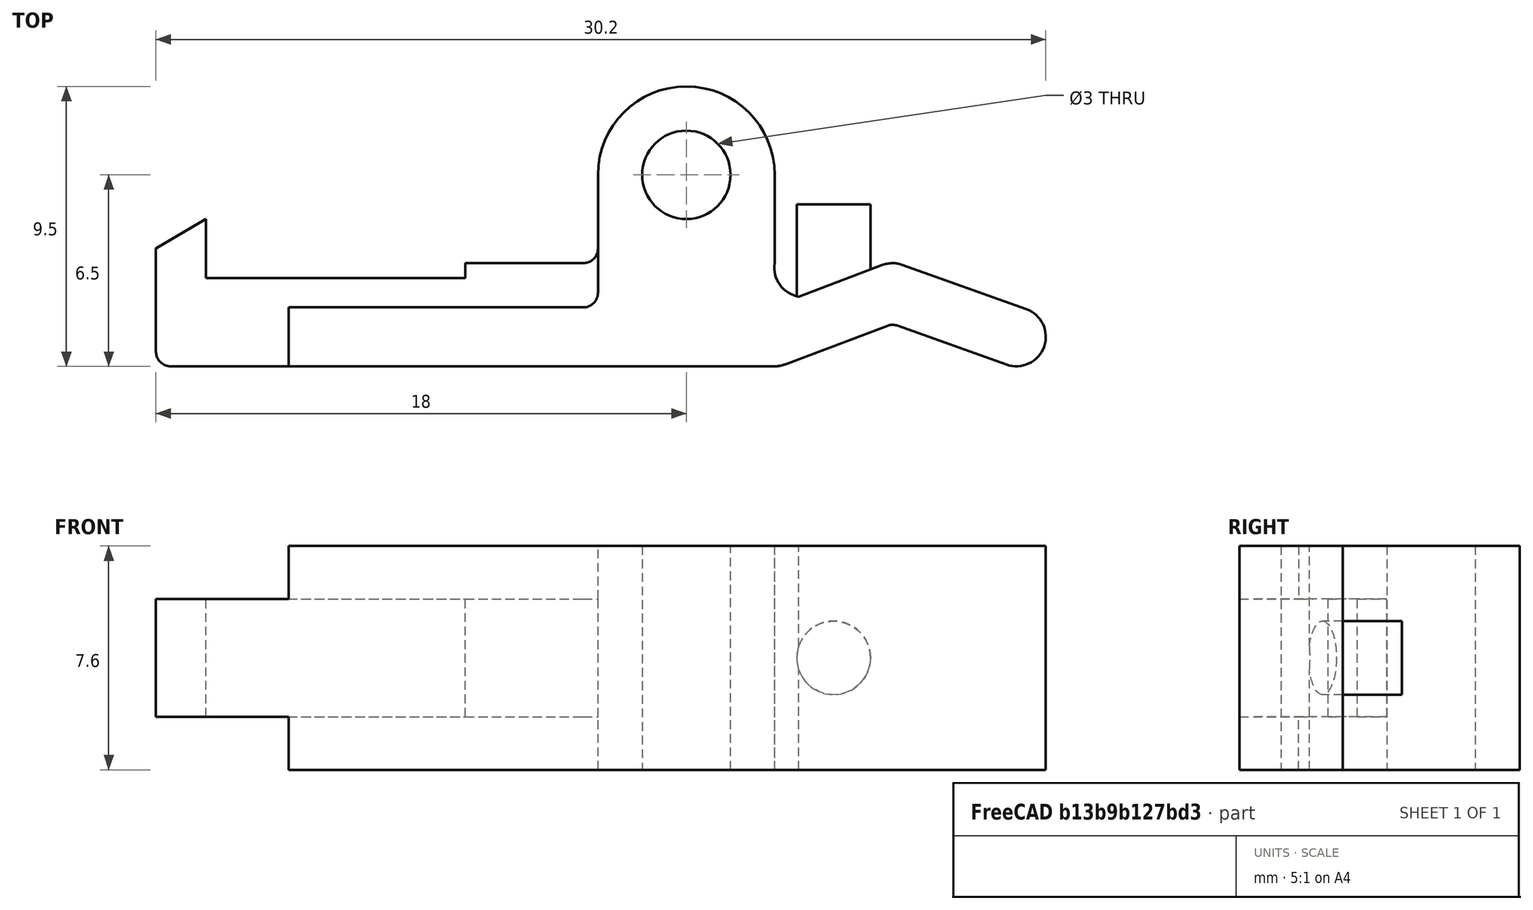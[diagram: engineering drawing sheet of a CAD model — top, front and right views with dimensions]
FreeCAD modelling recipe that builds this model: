
FCSTD DOCUMENT  (FreeCAD 0.20R29177 (Git))
Label: efs26_gehaeuse_hebel.stl
License: All rights reserved
LicenseURL: http://en.wikipedia.org/wiki/All_rights_reserved
objects: Sketcher::SketchObject×4, PartDesign::Pad×2, PartDesign::Pocket×2, PartDesign::Body×1, Mesh::Feature×1
note: 13 computed .brp shape members not serialized (recipe doc carries the construction recipe); baked Part::Feature solids carry a one-line shape summary decoded from their .brp

FEATURE [Sketcher::SketchObject] Sketch
  FullyConstrained = true
  MapMode = 5
  Support = -> [XY_Plane]
  sketch-geometry (27):
    g0: LineSegment StartX=0 StartY=4 StartZ=0 EndX=0 EndY=0.5 EndZ=0
    g1: LineSegment StartX=0.5 StartY=0 StartZ=0 EndX=21 EndY=0 EndZ=0
    g2: LineSegment StartX=21.3533 StartY=0.0644891 StartZ=0 EndX=24.8234 EndY=1.37496 EndZ=0
    g3: LineSegment StartX=25.1682 StartY=1.37808 StartZ=0 EndX=28.8637 EndY=0.0582581 EndZ=0
    g4: LineSegment StartX=0 StartY=4 StartZ=0 EndX=1.7 EndY=5 EndZ=0
    g5: LineSegment StartX=1.7 StartY=5 StartZ=0 EndX=1.7 EndY=3 EndZ=0
    g6: LineSegment StartX=15 StartY=4 StartZ=0 EndX=15 EndY=6.5 EndZ=0
    g7: LineSegment StartX=21 StartY=6.5 StartZ=0 EndX=21 EndY=3.5 EndZ=0
    g8: LineSegment StartX=21.81 StartY=2.36422 StartZ=0 EndX=24.6467 EndY=3.43551 EndZ=0
    g9: LineSegment StartX=25.3363 StartY=3.44174 StartZ=0 EndX=29.5363 EndY=1.94174 EndZ=0
    g10: Circle CenterX=18 CenterY=6.5 CenterZ=0 NormalX=0 NormalY=0 NormalZ=1 AngleXU=0 Radius=1.5
    g11: ArcOfCircle CenterX=18 CenterY=6.5 CenterZ=0 NormalX=0 NormalY=0 NormalZ=1 AngleXU=0 Radius=3 StartAngle=7e-16 EndAngle=3.14159
    g12: LineSegment StartX=15 StartY=6.5 StartZ=0 EndX=21 EndY=6.5 EndZ=0
    g13: ArcOfCircle CenterX=0.5 CenterY=0.5 CenterZ=0 NormalX=0 NormalY=0 NormalZ=1 AngleXU=0 Radius=0.5 StartAngle=3.14159 EndAngle=4.71239
    g14: ArcOfCircle CenterX=25 CenterY=2.5 CenterZ=0 NormalX=0 NormalY=0 NormalZ=1 AngleXU=0 Radius=1 StartAngle=1.22777 EndAngle=1.93189
    g15: ArcOfCircle CenterX=29.2 CenterY=1 CenterZ=0 NormalX=0 NormalY=0 NormalZ=1 AngleXU=0 Radius=1 StartAngle=4.36937 EndAngle=7.51096
    g16: LineSegment StartX=29.5363 StartY=1.94174 StartZ=0 EndX=28.8637 EndY=0.0582581 EndZ=0
    g17: ArcOfCircle CenterX=25 CenterY=0.907207 CenterZ=0 NormalX=0 NormalY=0 NormalZ=1 AngleXU=0 Radius=0.5 StartAngle=1.22777 EndAngle=1.93189
    g18: LineSegment StartX=25 StartY=2.5 StartZ=0 EndX=25 EndY=0.907207 EndZ=0
    g19: ArcOfCircle CenterX=21 CenterY=1 CenterZ=0 NormalX=0 NormalY=0 NormalZ=1 AngleXU=0 Radius=1 StartAngle=4.71239 EndAngle=5.07348
    g20: LineSegment StartX=21 StartY=6.5 StartZ=0 EndX=21 EndY=0 EndZ=0
    g21: ArcOfCircle CenterX=21.9884 CenterY=3.34818 CenterZ=0 NormalX=0 NormalY=0 NormalZ=1 AngleXU=0 Radius=1 StartAngle=2.98918 EndAngle=4.53302
    g22: ArcOfCircle CenterX=14.5 CenterY=4 CenterZ=0 NormalX=0 NormalY=0 NormalZ=1 AngleXU=0 Radius=0.5 StartAngle=4.71239 EndAngle=6.28319
    g23: LineSegment StartX=14.5 StartY=3.5 StartZ=0 EndX=21 EndY=3.5 EndZ=0
    g24: LineSegment StartX=1.7 StartY=3 StartZ=0 EndX=10.5 EndY=3 EndZ=0
    g25: LineSegment StartX=10.5 StartY=3 StartZ=0 EndX=10.5 EndY=3.5 EndZ=0
    g26: LineSegment StartX=10.5 StartY=3.5 StartZ=0 EndX=14.5 EndY=3.5 EndZ=0
  constraints (71):
    c: Vertical(g0)
    c: Horizontal(g1)
    c: Coincident(g4,g0)
    c: Coincident(g5,g4)
    c: Coincident(g24,g5)
    c: Vertical(g6)
    c: Diameter(g10) = 3
    c: Coincident(g11,g10)
    c: Coincident(g11,g6)
    c: Coincident(g11,g7)
    c: Diameter(g11) = 6
    c: Coincident(g12,g6)
    c: Coincident(g12,g7)
    c: PointOnObject(g10,g12)
    c: DistanceY(g-1,g10) = 6.5
    c: Horizontal(g12)
    c: DistanceX(g-1,g10) = 18
    c: Parallel(g5,g-2)
    c: Tangent(g0,g13) = -1.5708
    c: Tangent(g1,g13) = -1.5708
    c: Radius(g13) = 0.5
    c: PointOnObject(g1,g-1)
    c: PointOnObject(g0,g-2)
    c: DistanceX(g-1,g5) = 1.7
    c: DistanceY(g-1,g4) = 5
    c: DistanceY(g-1,g0) = 4
    c: Tangent(g8,g14) = 1.5708
    c: Tangent(g9,g14) = 1.5708
    c: Radius(g14) = 1
    c: Tangent(g3,g15) = -1.5708
    c: Tangent(g9,g15) = 1.5708
    c: Radius(g15) = 1
    c: Coincident(g16,g9)
    c: Coincident(g16,g3)
    c: PointOnObject(g15,g16)
    c: DistanceY(g-1,g15) = 1
    c: DistanceX(g-1,g15) = 29.2
    c: DistanceY(g-1,g14) = 2.5
    c: Tangent(g2,g17) = 1.5708
    c: Tangent(g3,g17) = 1.5708
    c: Radius(g17) = 0.5
    c: Coincident(g18,g14)
    c: Coincident(g18,g17)
    c: Vertical(g18)
    c: DistanceX(g-1,g17) = 25
    c: Tangent(g1,g19) = -1.5708
    c: Tangent(g2,g19) = -1.5708
    c: Radius(g19) = 1
    c: Coincident(g1,g20)
    c: Coincident(g7,g20)
    c: PointOnObject(g7,g20)
    c: Vertical(g20)
    c: Coincident(g21,g7)
    c: Coincident(g21,g8)
    c: Radius(g21) = 1
    c: Parallel(g8,g2)
    c: Tangent(g26,g22) = -1.5708
    c: Tangent(g6,g22) = -1.5708
    c: Radius(g22) = 0.5
    c: DistanceY(g-1,g5) = 3
    c: Coincident(g23,g26)
    c: Coincident(g23,g7)
    c: Horizontal(g23)
    c: Coincident(g24,g25)
    c: Horizontal(g24)
    c: Coincident(g25,g26)
    c: Horizontal(g26)
    c: DistanceY(g-1,g22) = 3.5
    c: Vertical(g25)
    c: DistanceX(g-1,g24) = 10.5
    c: DistanceX(g-1,g8) = 21.81
FEATURE [PartDesign::Pad] Pad
  Direction = (0,0,1)
  Length = 7.6
  Length2 = 10
  Profile = -> Sketch
  ReferenceAxis = -> Sketch [N_Axis]
  Type = 0
FEATURE [Sketcher::SketchObject] Sketch001
  ExternalGeometry = -> [Pad]
  FullyConstrained = true
  MapMode = 5
  Support = -> [XY_Plane]
  sketch-geometry (7):
    g0: LineSegment StartX=0 StartY=6.5 StartZ=0 EndX=15 EndY=6.5 EndZ=0
    g1: LineSegment StartX=15 StartY=6.5 StartZ=0 EndX=15 EndY=2.5 EndZ=0
    g2: LineSegment StartX=0 StartY=6.5 StartZ=0 EndX=0 EndY=0 EndZ=0
    g3: LineSegment StartX=0 StartY=0 StartZ=0 EndX=4.5 EndY=0 EndZ=0
    g4: LineSegment StartX=4.5 StartY=0 StartZ=0 EndX=4.5 EndY=2 EndZ=0
    g5: LineSegment StartX=4.5 StartY=2 StartZ=0 EndX=14.5 EndY=2 EndZ=0
    g6: ArcOfCircle CenterX=14.5 CenterY=2.5 CenterZ=0 NormalX=0 NormalY=0 NormalZ=1 AngleXU=0 Radius=0.5 StartAngle=4.71239 EndAngle=6.28319
  constraints (18):
    c: PointOnObject(g0,g-2)
    c: Coincident(g0,g-4)
    c: Horizontal(g0)
    c: Coincident(g1,g0)
    c: PointOnObject(g-4,g1)
    c: Coincident(g4,g3)
    c: Vertical(g4)
    c: Coincident(g5,g4)
    c: Horizontal(g5)
    c: Horizontal(g3)
    c: DistanceX(g-1,g3) = 4.5
    c: DistanceY(g-1,g4) = 2
    c: Tangent(g1,g6) = 1.5708
    c: Tangent(g5,g6) = -1.5708
    c: Radius(g6) = 0.5
    c: Coincident(g2,g3)
    c: Coincident(g2,g-1)
    c: Coincident(g2,g0)
FEATURE [PartDesign::Pocket] Pocket
  BaseFeature = -> Pad
  Direction = (0,0,-1)
  Length = 1.8
  Length2 = 5
  Profile = -> Sketch001
  ReferenceAxis = -> Sketch001 [N_Axis]
  Reversed = true
  Type = 0
FEATURE [Sketcher::SketchObject] Sketch002
  AttachmentOffset = pos=(0,0,7.6) rot=(0,0,1;0rad)
  ExternalGeometry = -> [Pad]
  FullyConstrained = true
  MapMode = 5
  Placement = pos=(0,0,7.6) rot=(0,0,1;0rad)
  Support = -> [XY_Plane]
  sketch-geometry (7):
    g0: LineSegment StartX=0 StartY=6.5 StartZ=0 EndX=15 EndY=6.5 EndZ=0
    g1: LineSegment StartX=15 StartY=6.5 StartZ=0 EndX=15 EndY=2.5 EndZ=0
    g2: LineSegment StartX=0 StartY=6.5 StartZ=0 EndX=0 EndY=0 EndZ=0
    g3: LineSegment StartX=0 StartY=0 StartZ=0 EndX=4.5 EndY=0 EndZ=0
    g4: LineSegment StartX=4.5 StartY=0 StartZ=0 EndX=4.5 EndY=2 EndZ=0
    g5: LineSegment StartX=4.5 StartY=2 StartZ=0 EndX=14.5 EndY=2 EndZ=0
    g6: ArcOfCircle CenterX=14.5 CenterY=2.5 CenterZ=0 NormalX=0 NormalY=0 NormalZ=1 AngleXU=0 Radius=0.5 StartAngle=4.71239 EndAngle=6.28319
  constraints (18):
    c: PointOnObject(g0,g-2)
    c: Coincident(g0,g-4)
    c: Horizontal(g0)
    c: Coincident(g1,g0)
    c: PointOnObject(g-4,g1)
    c: Coincident(g4,g3)
    c: Vertical(g4)
    c: Coincident(g5,g4)
    c: Horizontal(g5)
    c: Horizontal(g3)
    c: DistanceX(g-1,g3) = 4.5
    c: DistanceY(g-1,g4) = 2
    c: Tangent(g1,g6) = 1.5708
    c: Tangent(g5,g6) = -1.5708
    c: Radius(g6) = 0.5
    c: Coincident(g2,g3)
    c: Coincident(g2,g-1)
    c: Coincident(g2,g0)
FEATURE [PartDesign::Pocket] Pocket001
  BaseFeature = -> Pocket
  Direction = (0,0,-1)
  Length = 1.8
  Length2 = 5
  Profile = -> Sketch002
  ReferenceAxis = -> Sketch002 [N_Axis]
  Type = 0
FEATURE [Sketcher::SketchObject] Sketch003
  AttachmentOffset = pos=(0,0,-1.5) rot=(0,0,1;0rad)
  FullyConstrained = true
  MapMode = 5
  Placement = pos=(0,1.5,-3e-16) rot=(1,0,0;1.5708rad)
  Support = -> [XZ_Plane]
  sketch-geometry (1):
    g0: Circle CenterX=23 CenterY=3.8 CenterZ=0 NormalX=0 NormalY=0 NormalZ=1 AngleXU=0 Radius=1.25
  constraints (3):
    c: Diameter(g0) = 2.5
    c: DistanceY(g-1,g0) = 3.8
    c: DistanceX(g-1,g0) = 23
FEATURE [PartDesign::Pad] Pad001
  BaseFeature = -> Pocket001
  Direction = (0,-1,2e-16)
  Length = 4
  Length2 = 10
  Profile = -> Sketch003
  ReferenceAxis = -> Sketch003 [N_Axis]
  Reversed = true
  Type = 0
FEATURE [PartDesign::Body] Body  label="Hebel"
  Group = -> [Sketch,Pad,Sketch001,Pocket,Sketch002,Pocket001,Sketch003,Pad001]
  Origin = -> Origin
  Tip = -> Pad001
FEATURE [Mesh::Feature] Mesh  label="Pad001 (Meshed)"
